# Revit family: BVN_ARMO-A
name_source: partatom
category: Mechanical Equipment
units: mm (PartAtom-declared; Revit-internal decimal feet)

## family parameters
Always vertical = Yes
Cut with Voids When Loaded = No
OmniClass Number = 23.75.00.00
OmniClass Title = Climate Control (HVAC)
Part Type = Normal
Room Calculation Point = No
Round Connector Dimension = Use Diameter
Shared = No
Work Plane-Based = No

## types (21) — shared parameters
Fitting = <By Category>
Main Body = <By Category>
t = 5 mm  [stored 0.0164042 ft]
t' = -5 mm  [stored -0.0164042 ft]

## per-type parameters (varying)
| type | Air Flow | Current | E | E' | Hf | HfL | K | L | Power | QDa | QDi | QDi' | QTk | Q_Bottom | Q_Top | Qd | Speed (rpm) | Wing Angle (degree) | e | e' |
| ARMO-A 400-6/0,75-2A | 5250 m³/h | 2 A | 335 mm  [stored 1.09908 ft] | 415 mm | 255 mm  [stored 0.836614 ft] | 60 mm  [stored 0.19685 ft] | 420 mm | 474 mm | 750 W | 480 mm | 400 mm | 390 mm | 225 mm  [stored 0.738189 ft] | 250 mm  [stored 0.82021 ft] | 200 mm  [stored 0.656168 ft] | 12 mm  [stored 0.0393701 ft] | 2900 | 16 | 208 mm | -208 mm |
| ARMO-A 450-6/1,1-2A | 6248 m³/h | 2 A | 385 mm | 465 mm | 280 mm  [stored 0.918635 ft] | 70 mm  [stored 0.229659 ft] | 420 mm | 474 mm | 1100 W | 530 mm | 450 mm | 440 mm | 250 mm  [stored 0.82021 ft] | 250 mm  [stored 0.82021 ft] | 200 mm  [stored 0.656168 ft] | 12 mm  [stored 0.0393701 ft] | 2900 | 10 | 233 mm | -233 mm |
| ARMO-A 500-6/3-2A | 13545 m³/h | 6 A | 425 mm | 505 mm | 310 mm  [stored 1.01706 ft] | 80 mm  [stored 0.262467 ft] | 524 mm | 580 mm | 3000 W | 590 mm | 500 mm | 490 mm | 280 mm  [stored 0.918635 ft] | 300 mm | 250 mm  [stored 0.82021 ft] | 12 mm  [stored 0.0393701 ft] | 2900 | 28 | 253 mm | -253 mm |
| ARMO-A 560-6/4-2A | 17850 m³/h | 7 A | 485 mm | 565 mm | 340 mm | 85 mm  [stored 0.278871 ft] | 524 mm | 580 mm | 4000 W | 650 mm | 560 mm | 550 mm | 310 mm  [stored 1.01706 ft] | 300 mm | 250 mm  [stored 0.82021 ft] | 12 mm  [stored 0.0393701 ft] | 2900 | 14 | 283 mm | -283 mm |
| ARMO-A 630-6/4-4A | 25200 m³/h | 8 A | 555 mm | 635 mm | 375 mm | 90 mm  [stored 0.295276 ft] | 544 mm | 600 mm | 4000 W | 720 mm | 630 mm | 620 mm | 345 mm | 320 mm  [stored 1.04987 ft] | 270 mm  [stored 0.885827 ft] | 12 mm  [stored 0.0393701 ft] | 1500 | 38 | 318 mm | -318 mm |
| ARMO-A 710-6/3-4A | 27825 m³/h | 7 A | 595 mm | 675 mm | 420 mm | 95 mm | 544 mm | 600 mm | 3000 W | 800 mm | 710 mm | 700 mm | 385 mm | 330 mm | 280 mm  [stored 0.918635 ft] | 12 mm  [stored 0.0393701 ft] | 1410 | 32 | 338 mm | -338 mm |
| ARMO-A 800-9/5,5-4A | 36488 m³/h | 11 A | 625 mm | 705 mm | 470 mm | 100 mm  [stored 0.328084 ft] | 634 mm | 700 mm | 5500 W | 890 mm | 800 mm | 790 mm | 430 mm | 360 mm | 300 mm | 12 mm  [stored 0.0393701 ft] | 1430 | 26 | 353 mm | -353 mm |
| ARMO-A 900-9/11-4A | 54600 m³/h | 21 A | 675 mm | 755 mm | 527 mm | 110 mm  [stored 0.360892 ft] | 697 mm | 775 mm | 11000 W | 1005 mm | 900 mm | 890 mm | 485 mm | 400 mm | 350 mm | 15 mm  [stored 0.0492126 ft] | 1450 | 26 | 378 mm | -378 mm |
| ARMO-A 1000-9/15-4A | 69300 m³/h | 29 A | 775 mm | 855 mm | 577 mm | 130 mm  [stored 0.426509 ft] | 772 mm | 850 mm | 15000 W | 1105 mm | 1000 mm | 990 mm | 535 mm | 430 mm | 380 mm | 15 mm  [stored 0.0492126 ft] | 1450 | 24 | 428 mm | -428 mm |
| ARMO-A 1250-9/30-4A | 114975 m³/h | 55 A | 950 mm | 1030 mm | 720 mm | 150 mm | 861 mm | 949 mm | 30000 W | 1390 mm | 1250 mm | 1240 mm | 660 mm | 500 mm | 450 mm | 15 mm  [stored 0.0492126 ft] | 1460 | 18 | 515 mm | -515 mm  [stored -1.68963 ft] |
| ARMO-A 500-6/1,1-4A | 12600 m³/h | 3 A | 425 mm | 505 mm | 310 mm  [stored 1.01706 ft] | 80 mm  [stored 0.262467 ft] | 524 mm | 580 mm | 1100 W | 590 mm | 500 mm | 490 mm | 280 mm  [stored 0.918635 ft] | 300 mm | 250 mm  [stored 0.82021 ft] | 12 mm  [stored 0.0393701 ft] | 1400 | 38 | 253 mm | -253 mm |
| ARMO-A 560-6/2,2-4A | 17850 m³/h | 5 A | 485 mm | 565 mm | 340 mm | 85 mm  [stored 0.278871 ft] | 524 mm | 580 mm | 2200 W | 650 mm | 560 mm | 550 mm | 310 mm  [stored 1.01706 ft] | 300 mm | 250 mm  [stored 0.82021 ft] | 12 mm  [stored 0.0393701 ft] | 1410 | 38 | 283 mm | -283 mm |
| ARMO-A 630-6/7,5-2A | 27300 m³/h | 14 A | 555 mm | 635 mm | 375 mm | 90 mm  [stored 0.295276 ft] | 544 mm | 600 mm | 7500 W | 720 mm | 630 mm | 620 mm | 345 mm | 320 mm  [stored 1.04987 ft] | 270 mm  [stored 0.885827 ft] | 12 mm  [stored 0.0393701 ft] | 2800 | 16 | 318 mm | -318 mm |
| ARMO-A 560-6/0,55-6A | 11576 m³/h | 1 A | 425 mm | 505 mm | 310 mm  [stored 1.01706 ft] | 80 mm  [stored 0.262467 ft] | 524 mm | 580 mm | 370 W | 590 mm | 500 mm | 490 mm | 280 mm  [stored 0.918635 ft] | 300 mm | 250 mm  [stored 0.82021 ft] | 12 mm  [stored 0.0393701 ft] | 930 | 22 | 253 mm | -253 mm |
| ARMO-A 500-6/0.37-6A | 8400 m³/h | 1 A | 425 mm | 505 mm | 310 mm  [stored 1.01706 ft] | 80 mm  [stored 0.262467 ft] | 524 mm | 580 mm | 370 W | 590 mm | 500 mm | 490 mm | 280 mm  [stored 0.918635 ft] | 300 mm | 250 mm  [stored 0.82021 ft] | 12 mm  [stored 0.0393701 ft] | 900 | 38 | 253 mm | -253 mm |
| ARMO-A 630-6/1,1-6A | 16800 m³/h | 3 A | 555 mm | 635 mm | 375 mm | 90 mm  [stored 0.295276 ft] | 544 mm | 600 mm | 1100 W | 720 mm | 630 mm | 620 mm | 345 mm | 320 mm  [stored 1.04987 ft] | 270 mm  [stored 0.885827 ft] | 12 mm  [stored 0.0393701 ft] | 945 | 38 | 318 mm | -318 mm |
| ARMO-A 710-6/4-6A | 21000 m³/h | 9 A | 595 mm | 675 mm | 420 mm | 95 mm | 544 mm | 600 mm | 4000 W | 800 mm | 710 mm | 700 mm | 385 mm | 330 mm | 280 mm  [stored 0.918635 ft] | 12 mm  [stored 0.0393701 ft] | 955 | 32 | 338 mm | -338 mm |
| ARMO-A 800-9/3-6A | 28350 m³/h | 7 A | 625 mm | 705 mm | 470 mm | 100 mm  [stored 0.328084 ft] | 634 mm | 700 mm | 3000 W | 890 mm | 800 mm | 790 mm | 430 mm | 360 mm | 300 mm | 12 mm  [stored 0.0393701 ft] | 950 | 32 | 353 mm | -353 mm |
| ARMO-A 900-9/4-6A | 39900 m³/h | 9 A | 675 mm | 755 mm | 527 mm | 110 mm  [stored 0.360892 ft] | 697 mm | 775 mm | 4000 W | 1005 mm | 900 mm | 890 mm | 485 mm | 400 mm | 350 mm | 15 mm  [stored 0.0492126 ft] | 955 | 30 | 378 mm | -378 mm |
| ARMO-A 1000-9/7,5-6A | 57750 m³/h | 15 A | 775 mm | 855 mm | 577 mm | 130 mm  [stored 0.426509 ft] | 772 mm | 850 mm | 5500 W | 1105 mm | 1000 mm | 990 mm | 535 mm | 430 mm | 380 mm | 15 mm  [stored 0.0492126 ft] | 960 | 32 | 428 mm | -428 mm |
| ARMO-A 1250-9/15-6A | 105000 m³/h | 29 A | 950 mm | 1030 mm | 720 mm | 150 mm | 861 mm | 949 mm | 15000 W | 1390 mm | 1250 mm | 1240 mm | 660 mm | 500 mm | 450 mm | 15 mm  [stored 0.0492126 ft] | 965 | 28 | 515 mm | -515 mm  [stored -1.68963 ft] |

note: [stored X ft] marks values corroborated as IEEE doubles in the binary element streams (Revit-internal decimal feet)

## geometry (parser evidence)
native form markers: Sweep x2
no freeform markers — native parametric forms only
